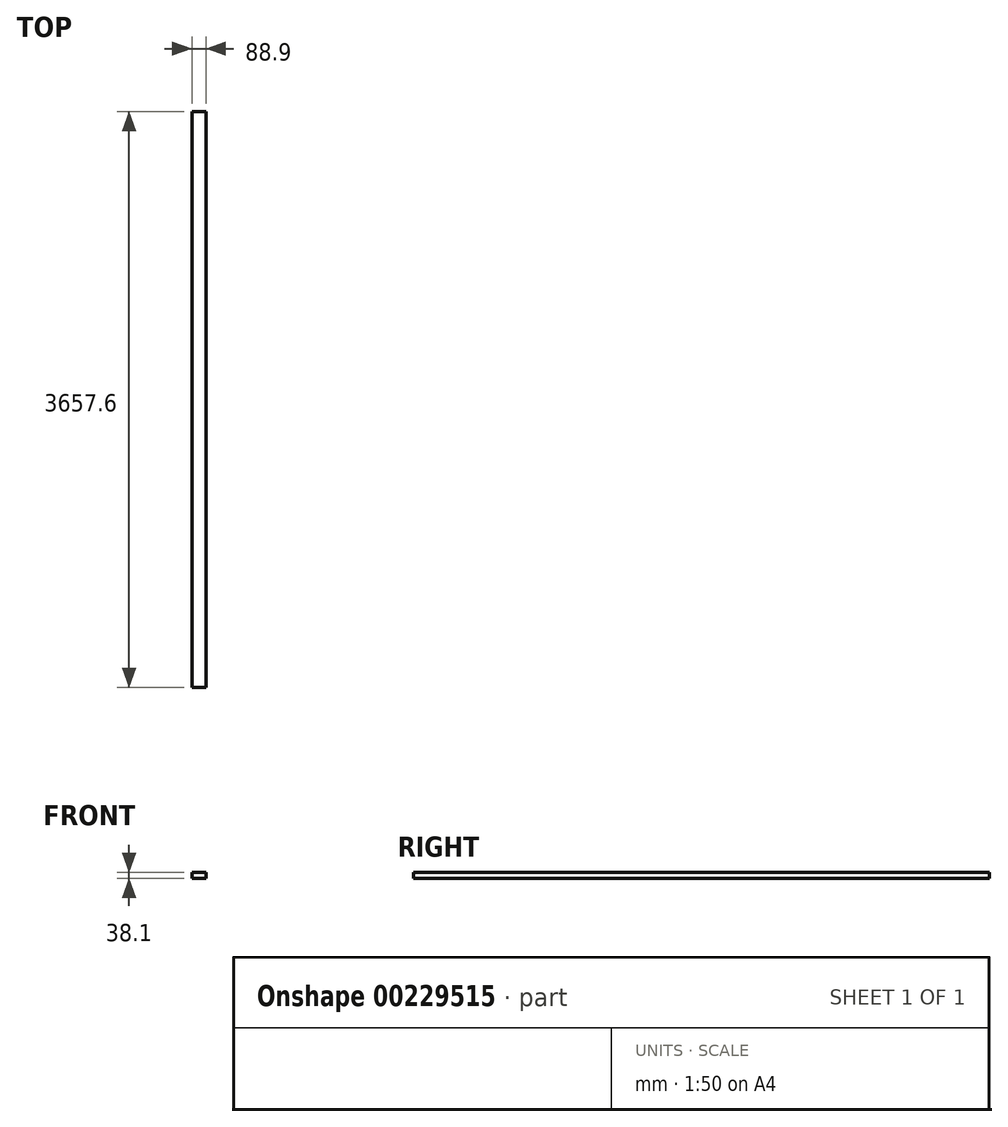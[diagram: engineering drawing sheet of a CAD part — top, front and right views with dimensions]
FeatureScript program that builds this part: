
annotation { "Feature Type Name" : "Feature", "Feature Type Description" : "" }
export const myFeature = defineFeature(function(context is Context, id is Id, definition is map)
    precondition{}
    {
        {
            var Q0;
            Q0=qCreatedBy(makeId("Front.planeOp"),FACE);
            var sketch = newSketch(context, id + "F0", { "sketchPlane" : qUnion([Q0])});
            skLineSegment(sketch, "E0.bottom", {"start": v(0, 0) * mm, "end": v(88.9, 0) * mm});
            skLineSegment(sketch, "E0.top", {"start": v(0, -38.1) * mm, "end": v(88.9, -38.1) * mm});
            skLineSegment(sketch, "E0.left", {"start": v(0, 0) * mm, "end": v(0, -38.1) * mm});
            skLineSegment(sketch, "E0.right", {"start": v(88.9, 0) * mm, "end": v(88.9, -38.1) * mm});
            skSolve(sketch);
        }
        {
            var Q0;
            Q0=qSketchRegion(id+"F0",true);
            extrude(context, id + "F1", {"entities" : qUnion([Q0]), "depth" : 3657.6 * mm});
        }
    });
